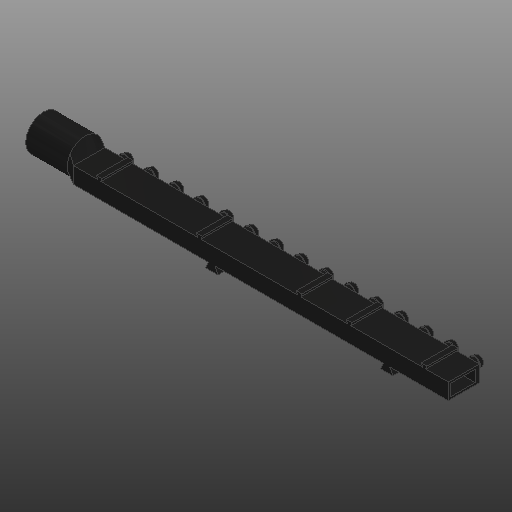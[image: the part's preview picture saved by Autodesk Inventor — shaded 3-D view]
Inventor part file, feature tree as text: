
AUTODESK INVENTOR PART (.ipt)
format: ipt  version: 2020 (Build 240168000, 168)  size: 586,752 bytes
history: native  units: in
note: dims shown in document units (in); Inventor stores cm internally (conversion verified against a paired STEP export)
features: other x11, extrude x6, loft x3, pattern_linear x1, projected_geometry x1
ambient origin geometry x8: Origin, YZ Plane, XZ Plane, XY Plane, X Axis, Y Axis, Z Axis, Center Point
bodies: Solid1 (feature_tree)
feature tree (22):
  other  "CrossSection1"
  other  "Box Sketch"
  extrude  "Box"  Depth=0.1181in
  other  "Fitting Plane"
  other  "Fitting"
  loft  "Fitting Entrance Loft"
  pattern_linear  "Channel Repetition"  Spacing1=0.0787in  [1 undecoded]
  extrude  "Small Tabs"  TaperAngle=0.0deg  [1 undecoded]
  extrude  "Big Tabs"  Depth=0.251in
  other  "Mouthpiece Plane"
  other  "Mouthpiece Sketch"
  loft  "Mouthpiece Loft (outer)"
  loft  "Mouthpiece Loft (inner)"
  extrude  "Mouthpiece"  Depth=0.0492in
  extrude  "Connector"  Depth=0.0315in
  extrude  "Shorten"  Depth=0.0938in
  other  "Fitting Sketch"
  other  "Fitting Entrance Loft From"
  projected_geometry  "Projected Loop1"
  other  "Small Tab Sketch"
  other  "Fitting Entrance Loft To"
  other  "Big Tab Sketch"
note: 2 required parameter values undecoded (feature->parameter linkage not recoverable at this tier; creation-order binding heuristic only, values carry confidence <= 0.55)
